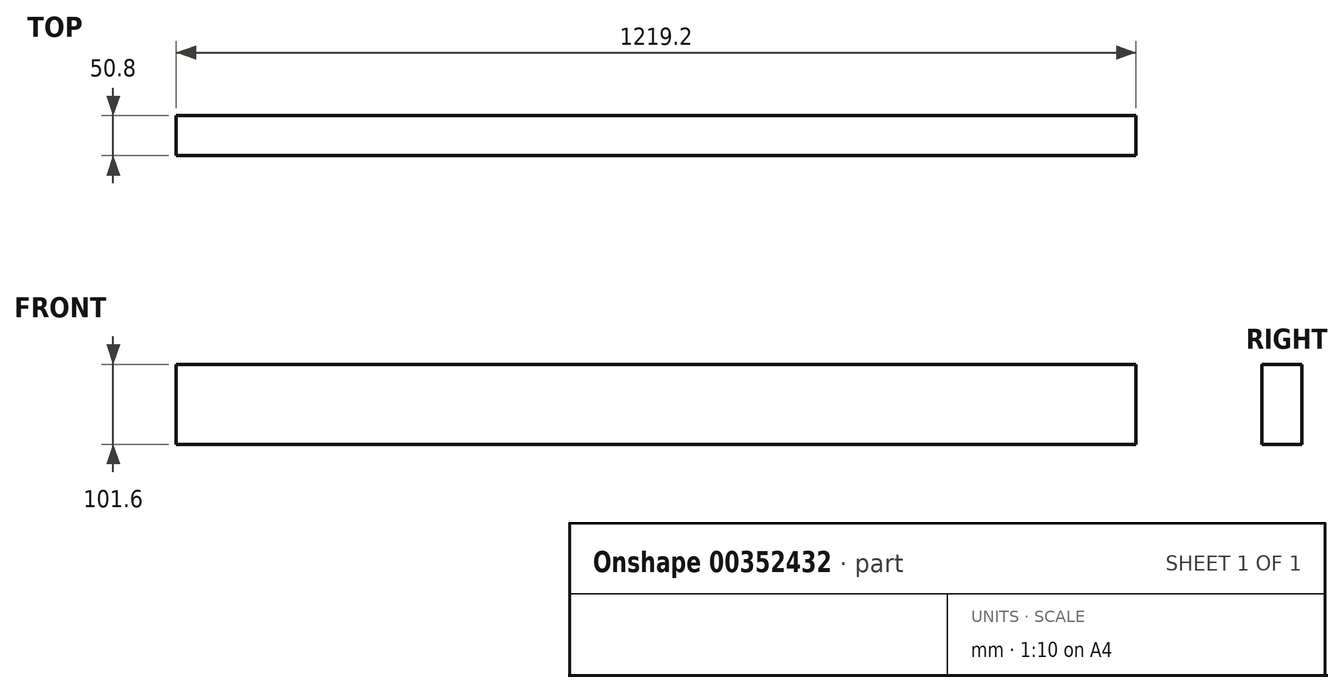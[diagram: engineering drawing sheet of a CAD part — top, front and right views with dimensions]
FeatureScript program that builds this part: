
annotation { "Feature Type Name" : "Feature", "Feature Type Description" : "" }
export const myFeature = defineFeature(function(context is Context, id is Id, definition is map)
    precondition{}
    {
        {
            var Q0;
            Q0=qCreatedBy(makeId("Right.planeOp"),FACE);
            var sketch = newSketch(context, id + "F0", { "sketchPlane" : qUnion([Q0])});
            skLineSegment(sketch, "E0.bottom", {"start": v(0, 0) * mm, "end": v(50.8, 0) * mm});
            skLineSegment(sketch, "E0.top", {"start": v(0, 101.6) * mm, "end": v(50.8, 101.6) * mm});
            skLineSegment(sketch, "E0.left", {"start": v(0, 0) * mm, "end": v(0, 101.6) * mm});
            skLineSegment(sketch, "E0.right", {"start": v(50.8, 0) * mm, "end": v(50.8, 101.6) * mm});
            skSolve(sketch);
        }
        {
            var Q0;
            Q0=makeQuery(id+"F0.imprint","IMPRINT",FACE,{"disambiguationData":[TD([[makeQuery(id+"F0.imprint","IMPRINT",EDGE,{"derivedFrom":sQuery(id+"F0.wireOp",EDGE,"E0.bottom")}),1.0]])]});
            extrude(context, id + "F1", {"entities" : qUnion([Q0]), "depth" : 1219.2 * mm});
        }
    });
